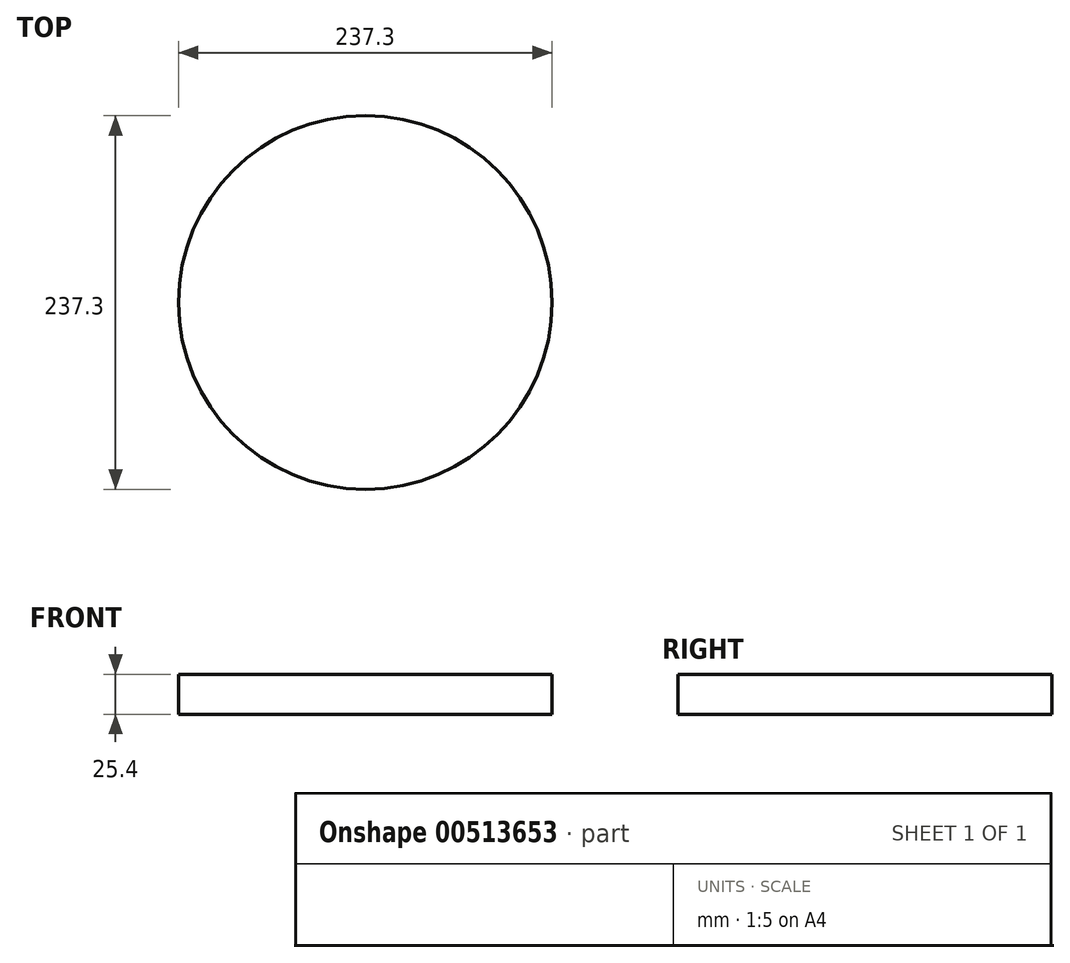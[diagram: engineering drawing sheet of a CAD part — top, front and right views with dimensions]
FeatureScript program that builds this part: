
annotation { "Feature Type Name" : "Feature", "Feature Type Description" : "" }
export const myFeature = defineFeature(function(context is Context, id is Id, definition is map)
    precondition{}
    {
        {
            var Q0;
            Q0=qCreatedBy(makeId("Top.planeOp"),FACE);
            var sketch = newSketch(context, id + "F0", { "sketchPlane" : qUnion([Q0])});
            skCircle(sketch, "E0", {"center": v(0, 0) * mm, "radius": 118.65 * mm});
            skSolve(sketch);
        }
        {
            var Q0;
            Q0=sQuery(id+"F0.wireOp",EDGE,"E0");
            extrude(context, id + "F1", {"bodyType" : ToolBodyType.SURFACE, "surfaceEntities" : qUnion([Q0]), "depth" : 25.4 * mm});
        }
    });
